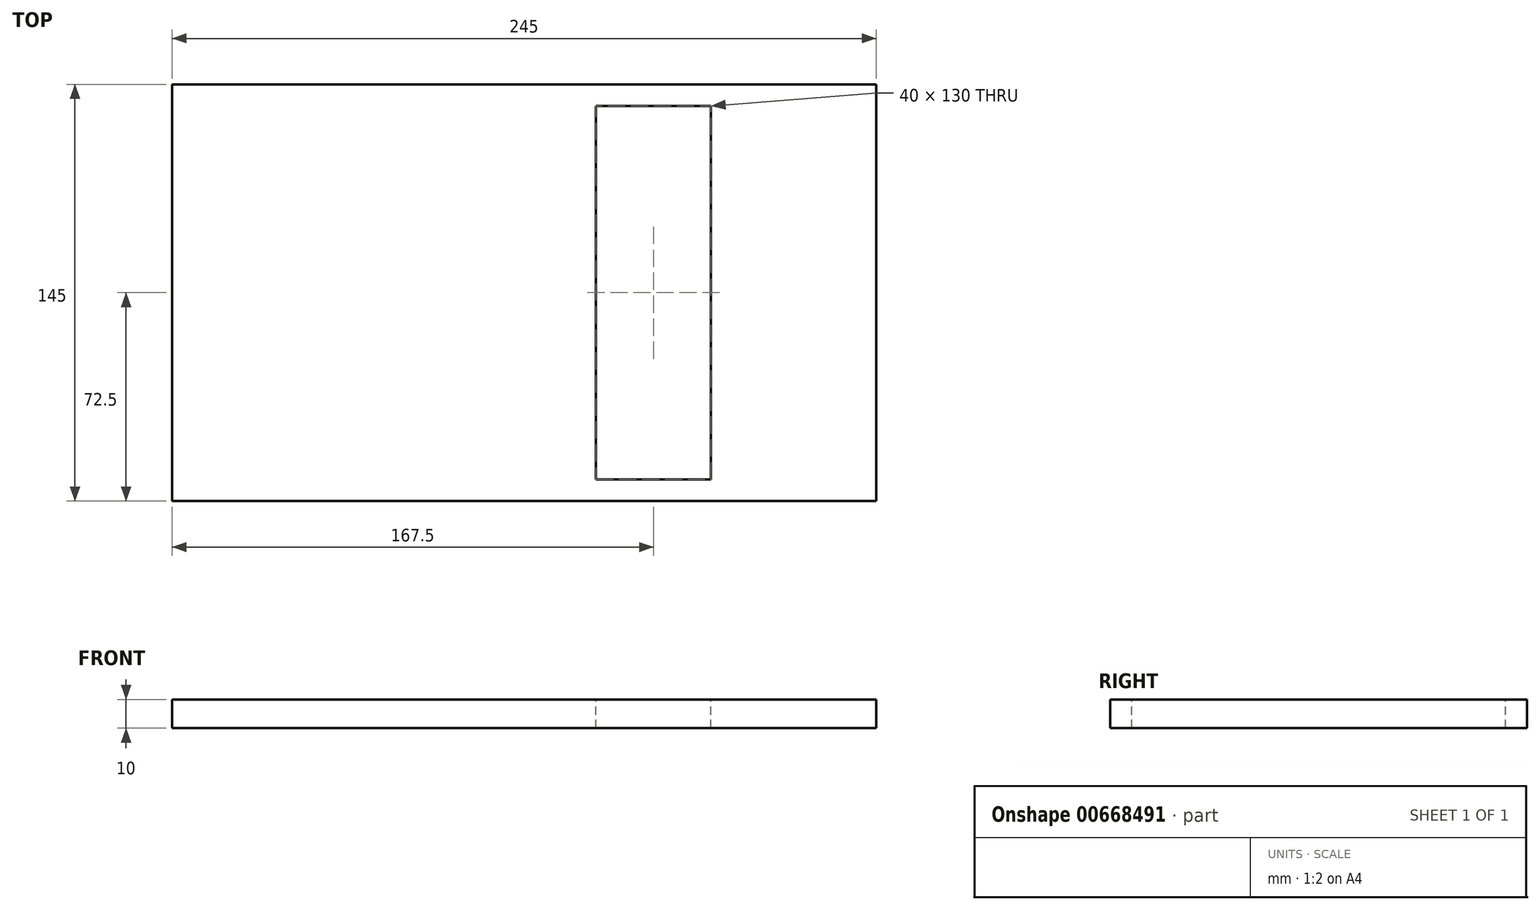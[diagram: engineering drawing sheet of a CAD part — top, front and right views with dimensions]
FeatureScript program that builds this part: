
annotation { "Feature Type Name" : "Feature", "Feature Type Description" : "" }
export const myFeature = defineFeature(function(context is Context, id is Id, definition is map)
    precondition{}
    {
        {
            var Q0;
            Q0=qCreatedBy(makeId("Top.planeOp"),FACE);
            var sketch = newSketch(context, id + "F0", { "sketchPlane" : qUnion([Q0])});
            skLineSegment(sketch, "E0.bottom", {"start": v(122.5, 72.5) * mm, "end": v(-122.5, 72.5) * mm});
            skLineSegment(sketch, "E0.top", {"start": v(122.5, -72.5) * mm, "end": v(-122.5, -72.5) * mm});
            skLineSegment(sketch, "E0.left", {"start": v(122.5, 72.5) * mm, "end": v(122.5, -72.5) * mm});
            skLineSegment(sketch, "E0.right", {"start": v(-122.5, 72.5) * mm, "end": v(-122.5, -72.5) * mm});
            skPoint(sketch, "E0.middle", {"position": v(0, 0) * mm});
            skSolve(sketch);
        }
        {
            var Q0;
            Q0=makeQuery(id+"F0.imprint","IMPRINT",FACE,{"disambiguationData":[TD([[makeQuery(id+"F0.imprint","IMPRINT",EDGE,{"derivedFrom":sQuery(id+"F0.wireOp",EDGE,"E0.bottom")}),1.0]])]});
            extrude(context, id + "F1", {"entities" : qUnion([Q0]), "depth" : 10 * mm, "offsetDistance" : 25 * mm});
        }
        {
            var Q0;
            Q0=makeQuery(id+"F1.opExtrude","CAP_FACE",FACE,{"disambiguationData":[OSD([sQuery(id+"F0.wireOp",EDGE,"E0.bottom"),sQuery(id+"F0.wireOp",EDGE,"E0.top"),sQuery(id+"F0.wireOp",EDGE,"E0.left"),sQuery(id+"F0.wireOp",EDGE,"E0.right")])],"isStart":false});
            var sketch = newSketch(context, id + "F2", { "sketchPlane" : qUnion([Q0])});
            skLineSegment(sketch, "E1", {"start": v(0, 0) * mm, "end": v(45, 0) * mm});
            skLineSegment(sketch, "E2.bottom", {"start": v(65, 65) * mm, "end": v(25, 65) * mm});
            skLineSegment(sketch, "E2.top", {"start": v(65, -65) * mm, "end": v(25, -65) * mm});
            skLineSegment(sketch, "E2.left", {"start": v(65, 65) * mm, "end": v(65, -65) * mm});
            skLineSegment(sketch, "E2.right", {"start": v(25, 65) * mm, "end": v(25, -65) * mm});
            skPoint(sketch, "E2.middle", {"position": v(45, 0) * mm});
            skSolve(sketch);
        }
        {
            var Q0;
            {var subQ1=sQuery(id+"F2.wireOp",EDGE,"E2.bottom");Q0=makeQuery(id+"F2.imprint","IMPRINT",FACE,{"disambiguationData":[TD([[makeQuery(id+"F2.imprint","IMPRINT",EDGE,{"derivedFrom":subQ1}),1.0]])]});}
            extrude(context, id + "F3", {"entities" : qUnion([Q0]), "operationType" : NewBodyOperationType.REMOVE, "oppositeDirection" : true, "depth" : 10 * mm, "offsetDistance" : 25 * mm});
        }
    });
